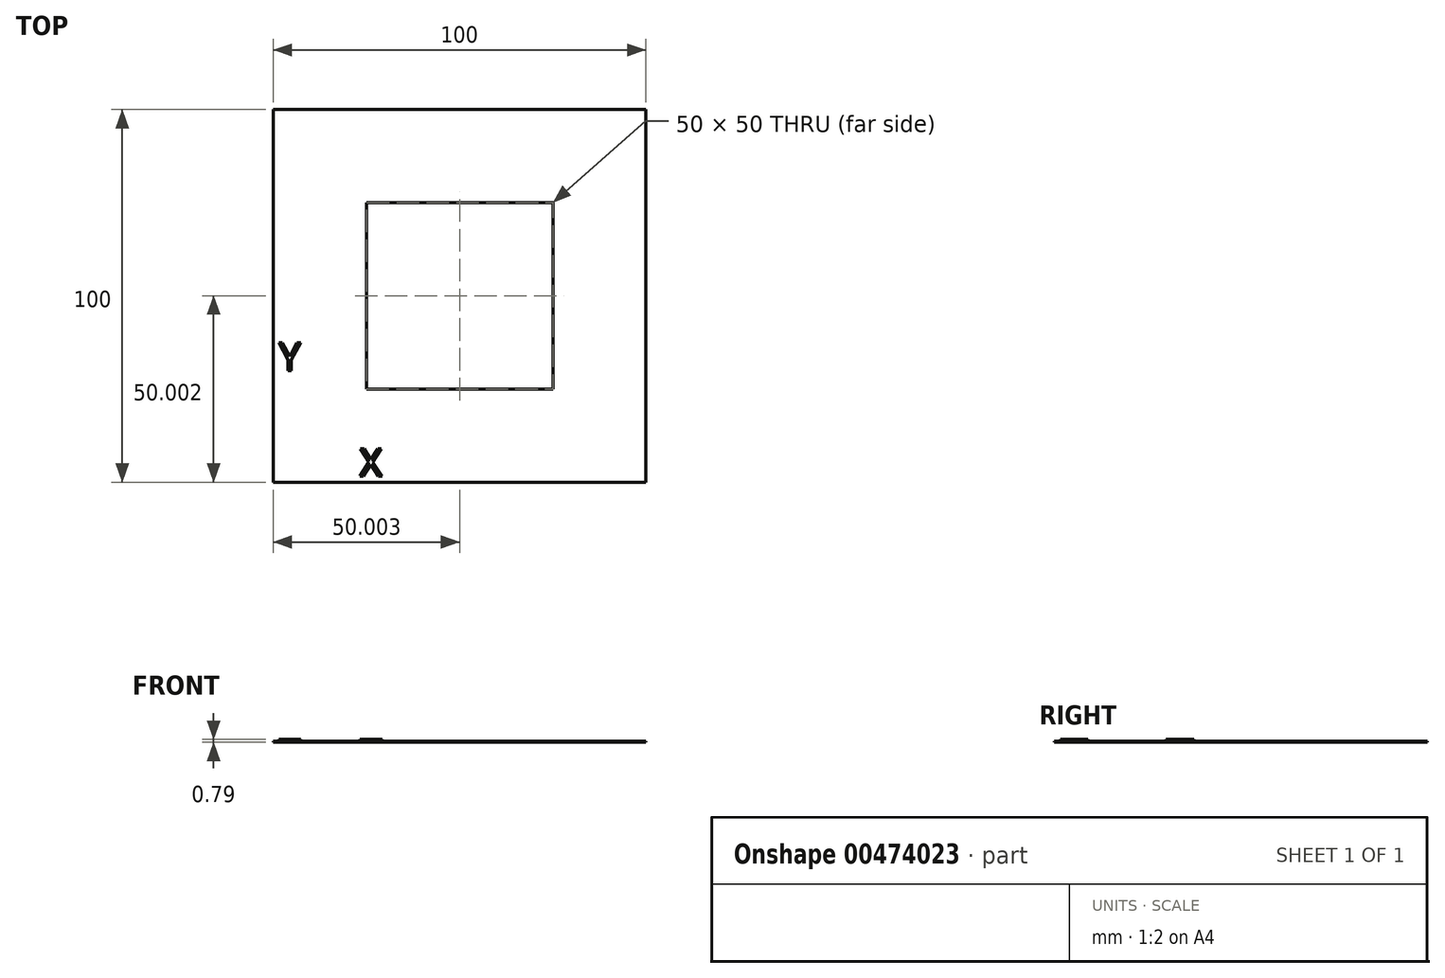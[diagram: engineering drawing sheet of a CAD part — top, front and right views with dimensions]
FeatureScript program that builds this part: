
annotation { "Feature Type Name" : "Feature", "Feature Type Description" : "" }
export const myFeature = defineFeature(function(context is Context, id is Id, definition is map)
    precondition{}
    {
        {
            var Q0;
            Q0=qCreatedBy(makeId("Top.planeOp"),FACE);
            var sketch = newSketch(context, id + "F0", { "sketchPlane" : qUnion([Q0])});
            skLineSegment(sketch, "E0.bottom", {"start": v(-35.72, 42.67) * mm, "end": v(64.28, 42.67) * mm});
            skLineSegment(sketch, "E0.top", {"start": v(-35.72, -57.33) * mm, "end": v(64.28, -57.33) * mm});
            skLineSegment(sketch, "E0.left", {"start": v(-35.72, 42.67) * mm, "end": v(-35.72, -57.33) * mm});
            skLineSegment(sketch, "E0.right", {"start": v(64.28, 42.67) * mm, "end": v(64.28, -57.33) * mm});
            skPoint(sketch, "E1", {"position": v(14.28, -7.33) * mm});
            skLineSegment(sketch, "E2.bottom", {"start": v(-10.72, 17.67) * mm, "end": v(39.28, 17.67) * mm});
            skLineSegment(sketch, "E2.top", {"start": v(-10.72, -32.33) * mm, "end": v(39.28, -32.33) * mm});
            skLineSegment(sketch, "E2.left", {"start": v(-10.72, 17.67) * mm, "end": v(-10.72, -32.33) * mm});
            skLineSegment(sketch, "E2.right", {"start": v(39.28, 17.67) * mm, "end": v(39.28, -32.33) * mm});
            skSolve(sketch);
        }
        {
            var Q0;
            Q0 = qSketchRegion(id + "F0", true);
            extrude(context, id + "F1", {"entities" : qUnion([Q0]), "depth" : .2625 * mm, "offsetDistance" : 25 * mm});
        }
        {
            var Q0;
            Q0=makeQuery(id+"F1.opExtrude","CAP_FACE",FACE,{"disambiguationData":[OSD([sQuery(id+"F0.wireOp",EDGE,"E0.bottom"),sQuery(id+"F0.wireOp",EDGE,"E0.top"),sQuery(id+"F0.wireOp",EDGE,"E0.left"),sQuery(id+"F0.wireOp",EDGE,"E0.right")])],"isStart":false});
            var sketch = newSketch(context, id + "F2", { "sketchPlane" : qUnion([Q0])});
            skPoint(sketch, "E3", {"position": v(14.28, -7.33) * mm});
            skText(sketch, "E4", { "text": "Y\n\n        X", "fontName": "OpenSans-Regular.ttf"});
            const initialGuessF2  = {"E4": [-0.03425, -0.02735, 1, 0, 0.00752]};
            skSetInitialGuess(sketch, initialGuessF2);
            skSolve(sketch);
        }
        {
            var Q0;
            Q0 = qSketchRegion(id + "F2", true);
            extrude(context, id + "F3", {"entities" : qUnion([Q0]), "operationType" : NewBodyOperationType.ADD, "depth" : .525 * mm});
        }
    });
